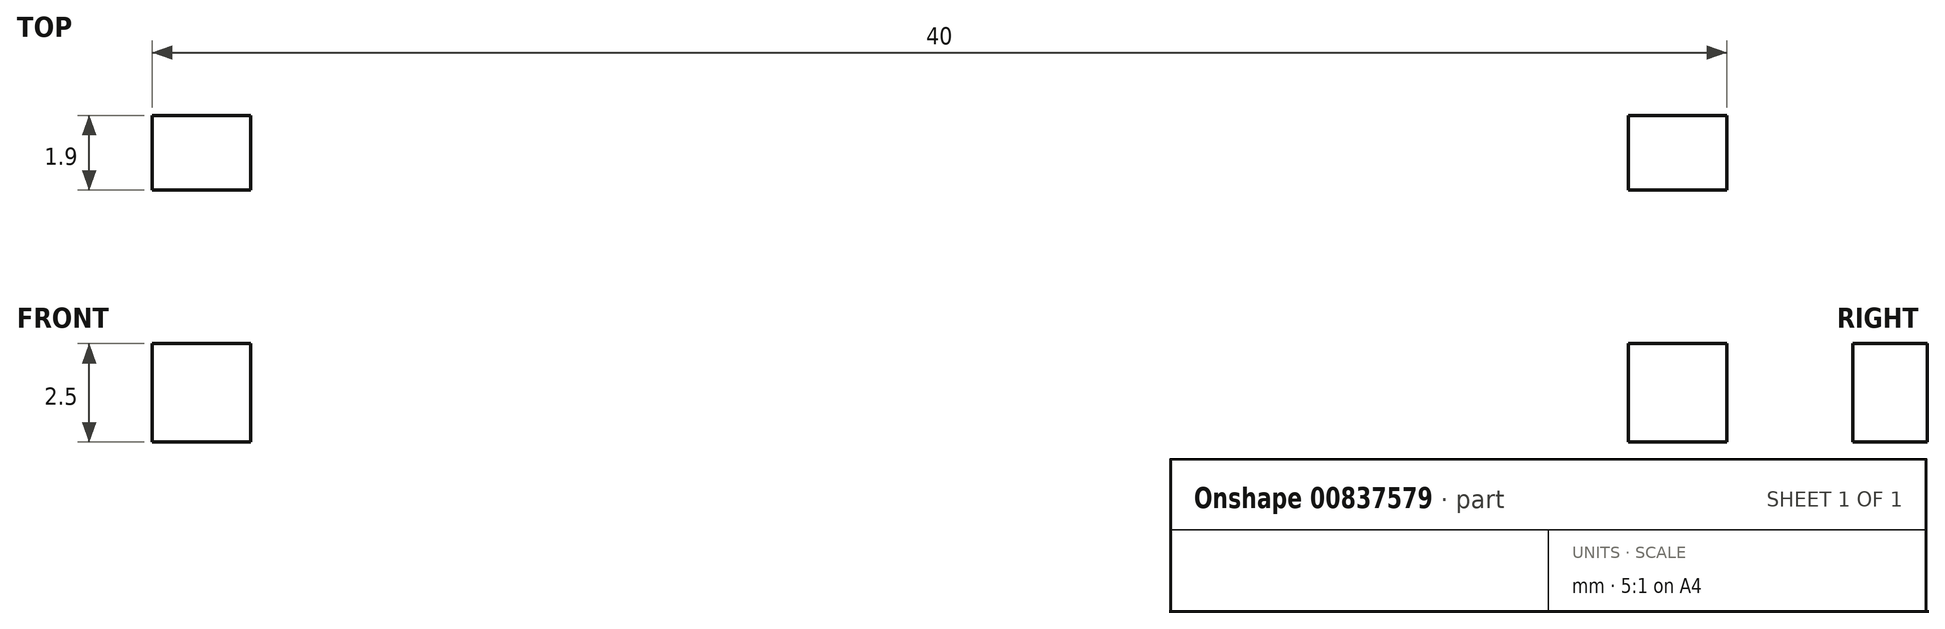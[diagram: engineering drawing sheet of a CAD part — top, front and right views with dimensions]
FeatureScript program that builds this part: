
annotation { "Feature Type Name" : "Feature", "Feature Type Description" : "" }
export const myFeature = defineFeature(function(context is Context, id is Id, definition is map)
    precondition{}
    {
        {
            var Q0;
            Q0=qCreatedBy(makeId("Front.planeOp"),FACE);
            var sketch = newSketch(context, id + "F0", { "sketchPlane" : qUnion([Q0])});
            skLineSegment(sketch, "E0.bottom", {"start": v(20, -17) * mm, "end": v(-20, -17) * mm});
            skLineSegment(sketch, "E0.top", {"start": v(20, 17) * mm, "end": v(-20, 17) * mm});
            skLineSegment(sketch, "E0.left", {"start": v(20, -17) * mm, "end": v(20, 17) * mm});
            skLineSegment(sketch, "E0.right", {"start": v(-20, -17) * mm, "end": v(-20, 17) * mm});
            skPoint(sketch, "E0.middle", {"position": v(0, 0) * mm});
            skLineSegment(sketch, "E1.bottom", {"start": v(-20, 17) * mm, "end": v(-17.5, 17) * mm});
            skLineSegment(sketch, "E1.top", {"start": v(-20, 14.5) * mm, "end": v(-17.5, 14.5) * mm});
            skLineSegment(sketch, "E1.left", {"start": v(-20, 17) * mm, "end": v(-20, 14.5) * mm});
            skLineSegment(sketch, "E1.right", {"start": v(-17.5, 17) * mm, "end": v(-17.5, 14.5) * mm});
            skLineSegment(sketch, "E2.bottom", {"start": v(-20, -17) * mm, "end": v(-17.5, -17) * mm});
            skLineSegment(sketch, "E2.top", {"start": v(-20, -14.5) * mm, "end": v(-17.5, -14.5) * mm});
            skLineSegment(sketch, "E2.left", {"start": v(-20, -17) * mm, "end": v(-20, -14.5) * mm});
            skLineSegment(sketch, "E2.right", {"start": v(-17.5, -17) * mm, "end": v(-17.5, -14.5) * mm});
            skLineSegment(sketch, "E3.bottom", {"start": v(20, 17) * mm, "end": v(17.5, 17) * mm});
            skLineSegment(sketch, "E3.top", {"start": v(20, 14.5) * mm, "end": v(17.5, 14.5) * mm});
            skLineSegment(sketch, "E3.left", {"start": v(20, 17) * mm, "end": v(20, 14.5) * mm});
            skLineSegment(sketch, "E3.right", {"start": v(17.5, 17) * mm, "end": v(17.5, 14.5) * mm});
            skLineSegment(sketch, "E4.bottom", {"start": v(20, -17) * mm, "end": v(17.5, -17) * mm});
            skLineSegment(sketch, "E4.top", {"start": v(20, -14.5) * mm, "end": v(17.5, -14.5) * mm});
            skLineSegment(sketch, "E4.left", {"start": v(20, -17) * mm, "end": v(20, -14.5) * mm});
            skLineSegment(sketch, "E4.right", {"start": v(17.5, -17) * mm, "end": v(17.5, -14.5) * mm});
            skSolve(sketch);
        }
        {
            var Q0;
            Q0=makeQuery(id+"F0.imprint","IMPRINT",FACE,{"disambiguationData":[TD([[makeQuery(id+"F0.imprint","IMPRINT",EDGE,{"derivedFrom":sQuery(id+"F0.wireOp",EDGE,"E0.bottom")}),-1.0]])]});
            extrude(context, id + "F1", {"entities" : qUnion([Q0]), "depth" : 1.9 * mm, "offsetDistance" : 25 * mm});
        }
    });
